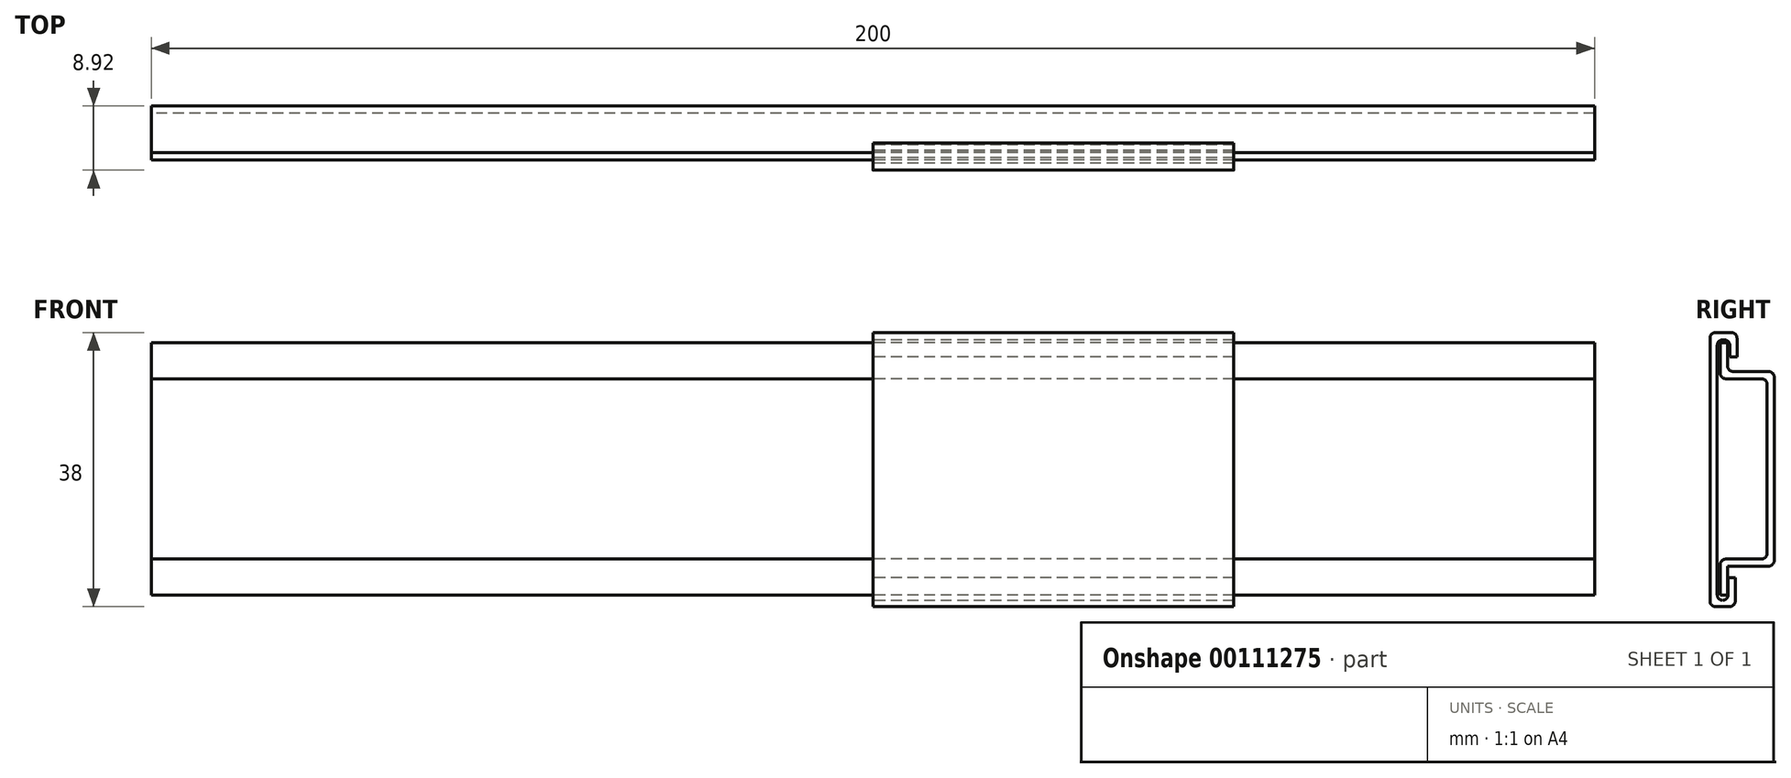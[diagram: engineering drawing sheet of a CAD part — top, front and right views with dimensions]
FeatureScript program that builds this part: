
annotation { "Feature Type Name" : "Feature", "Feature Type Description" : "" }
export const myFeature = defineFeature(function(context is Context, id is Id, definition is map)
    precondition{}
    {
        {
            var Q0;
            Q0=qCreatedBy(makeId("Right.planeOp"),FACE);
            var sketch = newSketch(context, id + "F0", { "sketchPlane" : qUnion([Q0])});
            skLineSegment(sketch, "E0", {"start": v(0, 16.6) * mm, "end": v(0, 11.6) * mm});
            skLineSegment(sketch, "E1", {"start": v(0, 11.6) * mm, "end": v(6.5, 11.6) * mm});
            skLineSegment(sketch, "E2", {"start": v(6.5, 11.6) * mm, "end": v(6.5, -13.4) * mm});
            skLineSegment(sketch, "E3", {"start": v(6.5, -13.4) * mm, "end": v(0, -13.4) * mm});
            skLineSegment(sketch, "E4", {"start": v(0, -13.4) * mm, "end": v(0, -18.4) * mm});
            skLineSegment(sketch, "E5", {"start": v(0, -18.4) * mm, "end": v(1, -18.4) * mm});
            skLineSegment(sketch, "E6", {"start": v(1, -18.4) * mm, "end": v(1, -14.4) * mm});
            skLineSegment(sketch, "E7", {"start": v(1, -14.4) * mm, "end": v(7.5, -14.4) * mm});
            skLineSegment(sketch, "E8", {"start": v(7.5, -14.4) * mm, "end": v(7.5, 12.6) * mm});
            skLineSegment(sketch, "E9", {"start": v(7.5, 12.6) * mm, "end": v(1, 12.6) * mm});
            skLineSegment(sketch, "E10", {"start": v(1, 12.6) * mm, "end": v(1, 16.6) * mm});
            skLineSegment(sketch, "E11", {"start": v(1, 16.6) * mm, "end": v(0, 16.6) * mm});
            skLineSegment(sketch, "E12", {"start": v(1.32, 14.6) * mm, "end": v(1.32, 17) * mm});
            skPoint(sketch, "E12.startSnap0", {"position": v(1, 14.6) * mm});
            skLineSegment(sketch, "E13", {"start": v(-0.42, 17) * mm, "end": v(-0.42, -19.12) * mm});
            skLineSegment(sketch, "E14", {"start": v(1.09, -19.12) * mm, "end": v(1.09, -16) * mm});
            skLineSegment(sketch, "E15", {"start": v(1.09, -16) * mm, "end": v(2.09, -16) * mm});
            skLineSegment(sketch, "E16", {"start": v(2.09, -16) * mm, "end": v(2.09, -20) * mm});
            skLineSegment(sketch, "E17", {"start": v(2.09, -20) * mm, "end": v(-1.42, -20) * mm});
            skLineSegment(sketch, "E18", {"start": v(-1.42, -20) * mm, "end": v(-1.42, 18) * mm});
            skLineSegment(sketch, "E19", {"start": v(-1.42, 18) * mm, "end": v(2.32, 18) * mm});
            skLineSegment(sketch, "E20", {"start": v(2.32, 18) * mm, "end": v(2.32, 14.6) * mm});
            skLineSegment(sketch, "E21", {"start": v(2.32, 14.6) * mm, "end": v(1.32, 14.6) * mm});
            skLineSegment(sketch, "E22", {"start": v(-0.42, 17) * mm, "end": v(1.32, 17) * mm});
            skLineSegment(sketch, "E23", {"start": v(1.09, -19.12) * mm, "end": v(-0.42, -19.12) * mm});
            skSolve(sketch);
        }
        {
            var Q0;
            Q0=makeQuery(id+"F0.imprint","IMPRINT",FACE,{"disambiguationData":[TD([[makeQuery(id+"F0.imprint","IMPRINT",EDGE,{"derivedFrom":sQuery(id+"F0.wireOp",EDGE,"E0")}),1.0]])]});
            extrude(context, id + "F1", {"entities" : qUnion([Q0]), "endBound" : BoundingType.SYMMETRIC, "depth" : 200 * mm});
        }
        {
            var Q0;
            Q0=makeQuery(id+"F1.opExtrude","SWEPT_EDGE",EDGE,{"disambiguationData":[OSD([sQuery(id+"F0.wireOp",EDGE,"E9"),sQuery(id+"F0.wireOp",EDGE,"E10")])]});
            var Q1;
            Q1=makeQuery(id+"F1.opExtrude","SWEPT_EDGE",EDGE,{"disambiguationData":[OSD([sQuery(id+"F0.wireOp",EDGE,"E0"),sQuery(id+"F0.wireOp",EDGE,"E1")])]});
            var Q2;
            Q2=makeQuery(id+"F1.opExtrude","SWEPT_EDGE",EDGE,{"disambiguationData":[OSD([sQuery(id+"F0.wireOp",EDGE,"E8"),sQuery(id+"F0.wireOp",EDGE,"E9")])]});
            var Q3;
            Q3=makeQuery(id+"F1.opExtrude","SWEPT_EDGE",EDGE,{"disambiguationData":[OSD([sQuery(id+"F0.wireOp",EDGE,"E1"),sQuery(id+"F0.wireOp",EDGE,"E2")])]});
            var Q4;
            Q4=makeQuery(id+"F1.opExtrude","SWEPT_EDGE",EDGE,{"disambiguationData":[OSD([sQuery(id+"F0.wireOp",EDGE,"E7"),sQuery(id+"F0.wireOp",EDGE,"E8")])]});
            var Q5;
            Q5=makeQuery(id+"F1.opExtrude","SWEPT_EDGE",EDGE,{"disambiguationData":[OSD([sQuery(id+"F0.wireOp",EDGE,"E3"),sQuery(id+"F0.wireOp",EDGE,"E4")])]});
            var Q6;
            Q6=makeQuery(id+"F1.opExtrude","SWEPT_EDGE",EDGE,{"disambiguationData":[OSD([sQuery(id+"F0.wireOp",EDGE,"E2"),sQuery(id+"F0.wireOp",EDGE,"E3")])]});
            fillet(context, id + "F2", {"entities" : qUnion([Q0, Q1, Q2, Q3, Q4, Q5, Q6]), "radius" : 0.8 * mm, "tangentPropagation" : true, "allowEdgeOverflow" : false});
        }
        {
            var Q0;
            Q0=makeQuery(id+"F0.imprint","IMPRINT",FACE,{"disambiguationData":[TD([[makeQuery(id+"F0.imprint","IMPRINT",EDGE,{"derivedFrom":sQuery(id+"F0.wireOp",EDGE,"E12")}),-1.0]])]});
            extrude(context, id + "F3", {"entities" : qUnion([Q0]), "operationType" : NewBodyOperationType.ADD, "depth" : 50 * mm});
        }
        {
            var Q0;
            Q0=makeQuery(id+"F3.opExtrude","SWEPT_EDGE",EDGE,{"disambiguationData":[OSD([sQuery(id+"F0.wireOp",EDGE,"E13"),sQuery(id+"F0.wireOp",EDGE,"E22")])]});
            var Q1;
            Q1=makeQuery(id+"F3.opExtrude","SWEPT_EDGE",EDGE,{"disambiguationData":[OSD([sQuery(id+"F0.wireOp",EDGE,"E18"),sQuery(id+"F0.wireOp",EDGE,"E19")])]});
            var Q2;
            Q2=makeQuery(id+"F3.opExtrude","SWEPT_EDGE",EDGE,{"disambiguationData":[OSD([sQuery(id+"F0.wireOp",EDGE,"E19"),sQuery(id+"F0.wireOp",EDGE,"E20")])]});
            var Q3;
            Q3=makeQuery(id+"F3.opExtrude","SWEPT_EDGE",EDGE,{"disambiguationData":[OSD([sQuery(id+"F0.wireOp",EDGE,"E12"),sQuery(id+"F0.wireOp",EDGE,"E22")])]});
            var Q4;
            Q4=makeQuery(id+"F3.opExtrude","SWEPT_EDGE",EDGE,{"disambiguationData":[OSD([sQuery(id+"F0.wireOp",EDGE,"E17"),sQuery(id+"F0.wireOp",EDGE,"E18")])]});
            var Q5;
            Q5=makeQuery(id+"F3.opExtrude","SWEPT_EDGE",EDGE,{"disambiguationData":[OSD([sQuery(id+"F0.wireOp",EDGE,"E16"),sQuery(id+"F0.wireOp",EDGE,"E17")])]});
            var Q6;
            Q6=makeQuery(id+"F3.opExtrude","SWEPT_EDGE",EDGE,{"disambiguationData":[OSD([sQuery(id+"F0.wireOp",EDGE,"E13"),sQuery(id+"F0.wireOp",EDGE,"E23")])]});
            var Q7;
            Q7=makeQuery(id+"F3.opExtrude","SWEPT_EDGE",EDGE,{"disambiguationData":[OSD([sQuery(id+"F0.wireOp",EDGE,"E14"),sQuery(id+"F0.wireOp",EDGE,"E23")])]});
            fillet(context, id + "F4", {"entities" : qUnion([Q0, Q1, Q2, Q3, Q4, Q5, Q6, Q7]), "radius" : 0.8 * mm, "tangentPropagation" : true, "allowEdgeOverflow" : false});
        }
    });
